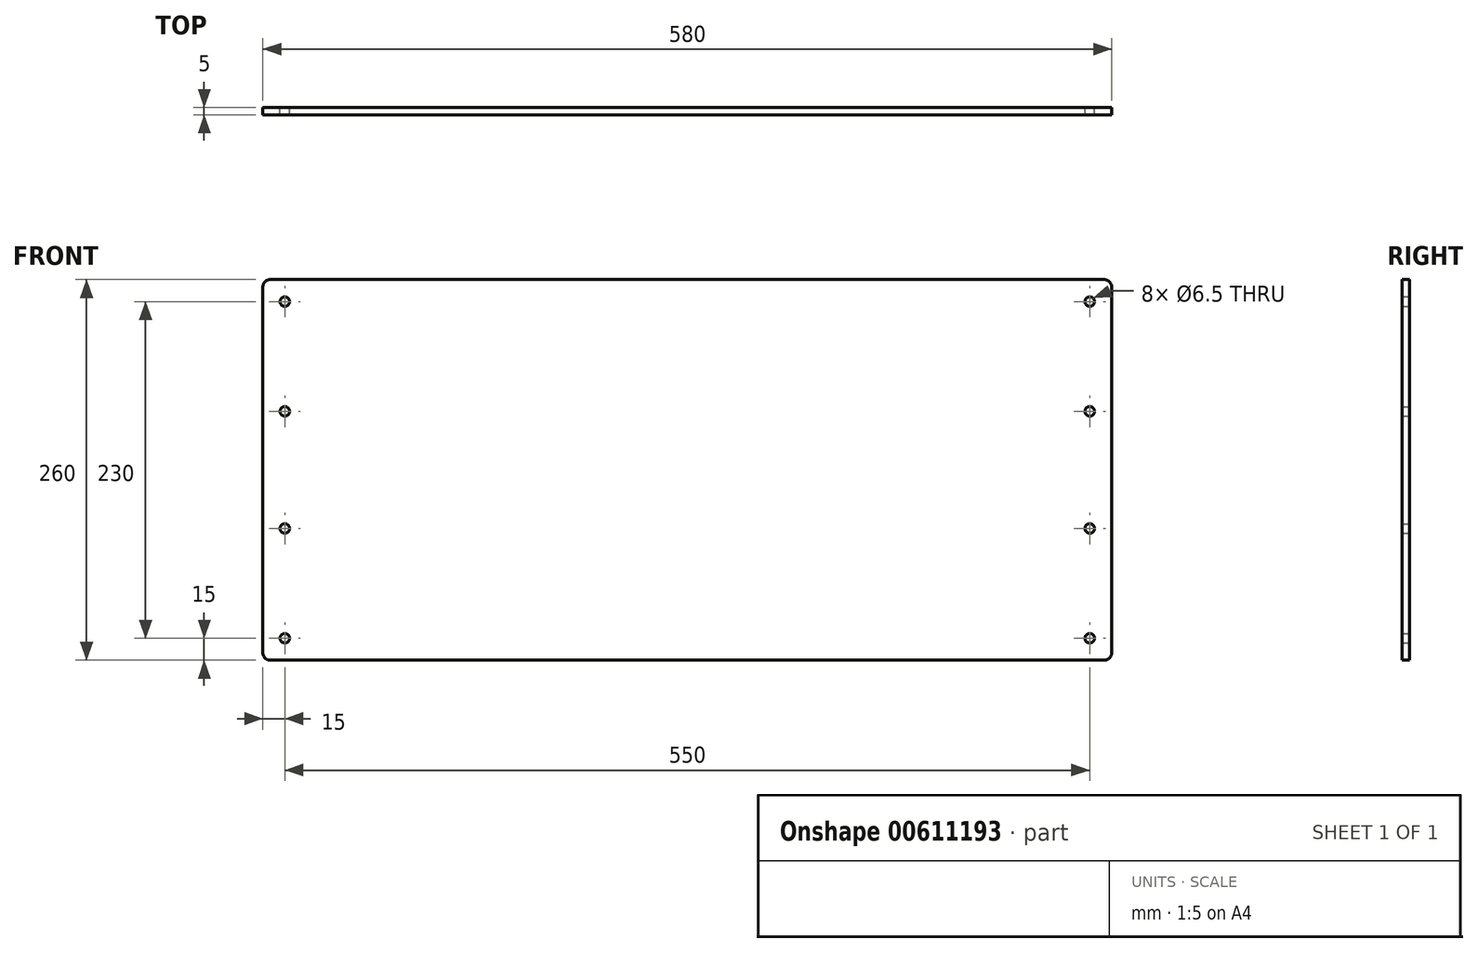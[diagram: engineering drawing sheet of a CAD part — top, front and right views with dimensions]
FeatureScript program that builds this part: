
annotation { "Feature Type Name" : "Feature", "Feature Type Description" : "" }
export const myFeature = defineFeature(function(context is Context, id is Id, definition is map)
    precondition{}
    {
        {
            var Q0;
            Q0=qCreatedBy(makeId("Front.planeOp"),FACE);
            var sketch = newSketch(context, id + "F0", { "sketchPlane" : qUnion([Q0])});
            skLineSegment(sketch, "E0.bottom", {"start": v(0, 0) * mm, "end": v(580, 0) * mm});
            skLineSegment(sketch, "E0.top", {"start": v(0, 260) * mm, "end": v(580, 260) * mm});
            skLineSegment(sketch, "E0.left", {"start": v(0, 0) * mm, "end": v(0, 260) * mm});
            skLineSegment(sketch, "E0.right", {"start": v(580, 0) * mm, "end": v(580, 260) * mm});
            skCircle(sketch, "E1", {"center": v(15, 15) * mm, "radius": 3.25 * mm});
            skCircle(sketch, "E2", {"center": v(15, 90) * mm, "radius": 3.25 * mm});
            skCircle(sketch, "E3", {"center": v(15, 170) * mm, "radius": 3.25 * mm});
            skCircle(sketch, "E4", {"center": v(15, 245) * mm, "radius": 3.25 * mm});
            skCircle(sketch, "E5", {"center": v(565, 15) * mm, "radius": 3.25 * mm});
            skCircle(sketch, "E6", {"center": v(565, 90) * mm, "radius": 3.25 * mm});
            skCircle(sketch, "E7", {"center": v(565, 170) * mm, "radius": 3.25 * mm});
            skCircle(sketch, "E8", {"center": v(565, 245) * mm, "radius": 3.25 * mm});
            skSolve(sketch);
        }
        {
            var Q0;
            Q0 = qSketchRegion(id + "F0", true);
            var Q1;
            Q1=makeQuery(id+"F0.imprint","IMPRINT",FACE,{"disambiguationData":[TD([[makeQuery(id+"F0.imprint","IMPRINT",EDGE,{"derivedFrom":sQuery(id+"F0.wireOp",EDGE,"E0.bottom")}),1.0]])]});
            extrude(context, id + "F1", {"entities" : qUnion([Q0, Q1]), "depth" : 5 * mm, "offsetDistance" : 25 * mm});
        }
        {
            var Q0;
            Q0=makeQuery(id+"F1.opExtrude","SWEPT_EDGE",EDGE,{"disambiguationData":[OSD([sQuery(id+"F0.wireOp",EDGE,"E0.top"),sQuery(id+"F0.wireOp",EDGE,"E0.left")])]});
            var Q1;
            Q1=makeQuery(id+"F1.opExtrude","SWEPT_EDGE",EDGE,{"disambiguationData":[OSD([sQuery(id+"F0.wireOp",EDGE,"E0.bottom"),sQuery(id+"F0.wireOp",EDGE,"E0.left")])]});
            var Q2;
            Q2=makeQuery(id+"F1.opExtrude","SWEPT_EDGE",EDGE,{"disambiguationData":[OSD([sQuery(id+"F0.wireOp",EDGE,"E0.top"),sQuery(id+"F0.wireOp",EDGE,"E0.right")])]});
            var Q3;
            Q3=makeQuery(id+"F1.opExtrude","SWEPT_EDGE",EDGE,{"disambiguationData":[OSD([sQuery(id+"F0.wireOp",EDGE,"E0.bottom"),sQuery(id+"F0.wireOp",EDGE,"E0.right")])]});
            fillet(context, id + "F2", {"entities" : qUnion([Q0, Q1, Q2, Q3]), "radius" : 5 * mm, "tangentPropagation" : true, "allowEdgeOverflow" : false});
        }
    });
